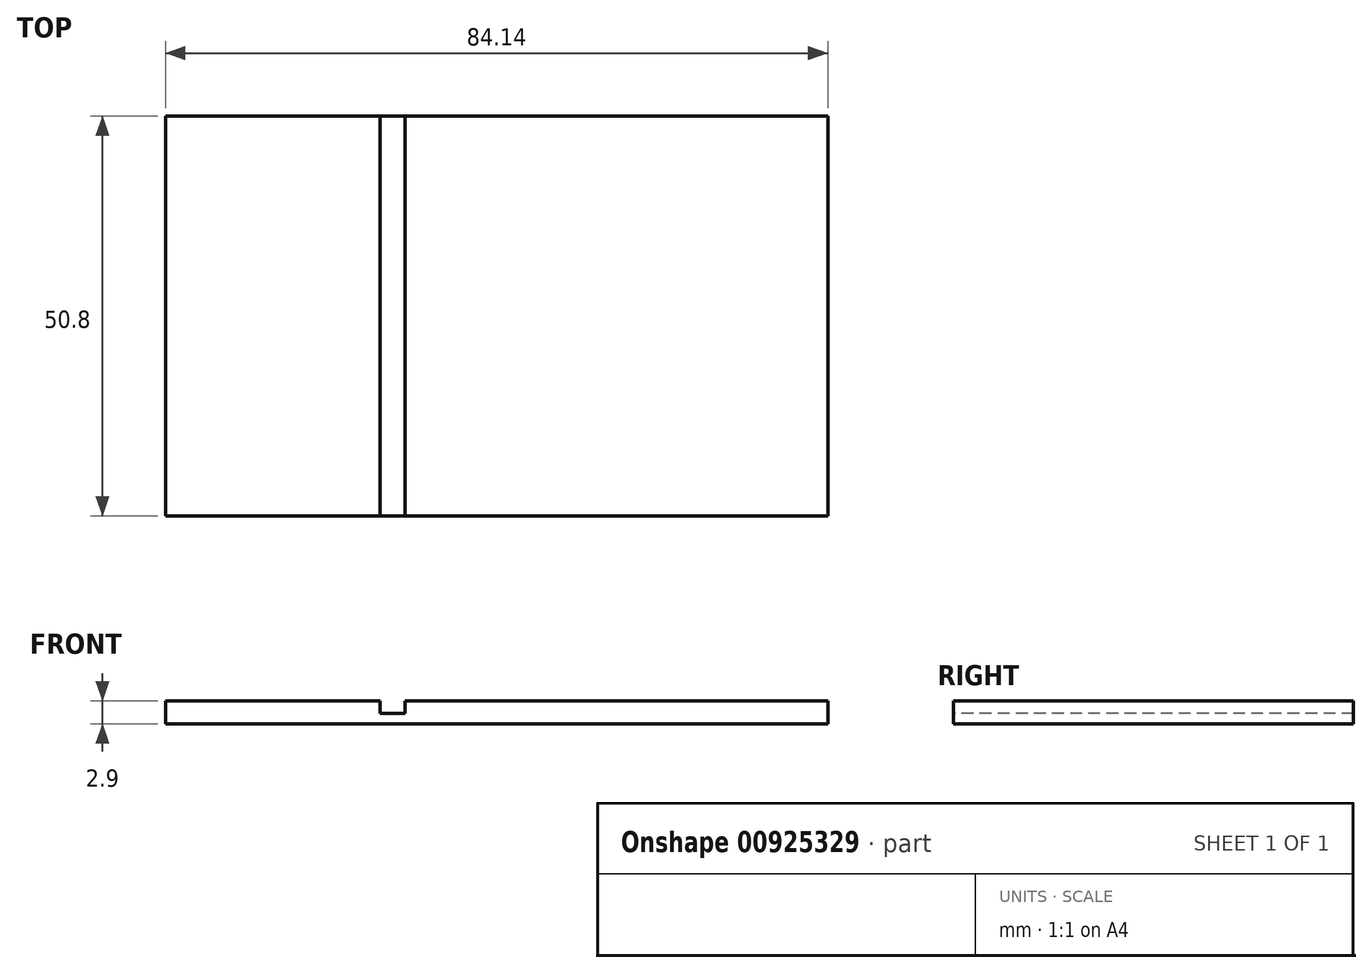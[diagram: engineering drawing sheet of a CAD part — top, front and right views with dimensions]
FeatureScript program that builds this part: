
annotation { "Feature Type Name" : "Feature", "Feature Type Description" : "" }
export const myFeature = defineFeature(function(context is Context, id is Id, definition is map)
    precondition{}
    {
        {
            var Q0;
            Q0=qCreatedBy(makeId("Top.planeOp"),FACE);
            var sketch = newSketch(context, id + "F0", { "sketchPlane" : qUnion([Q0])});
            skLineSegment(sketch, "E0.bottom", {"start": v(42.07, -25.4) * mm, "end": v(-42.07, -25.4) * mm});
            skLineSegment(sketch, "E0.top", {"start": v(42.07, 25.4) * mm, "end": v(-42.07, 25.4) * mm});
            skLineSegment(sketch, "E0.left", {"start": v(42.07, -25.4) * mm, "end": v(42.07, 25.4) * mm});
            skLineSegment(sketch, "E0.right", {"start": v(-42.07, -25.4) * mm, "end": v(-42.07, 25.4) * mm});
            skPoint(sketch, "E0.middle", {"position": v(0, 0) * mm});
            skSolve(sketch);
        }
        {
            var Q0;
            Q0=qSketchRegion(id+"F0",true);
            extrude(context, id + "F1", {"entities" : qUnion([Q0]), "depth" : 2.9 * mm, "offsetDistance" : 25.4 * mm});
        }
        {
            var Q0;
            Q0=makeQuery(id+"F1.opExtrude","CAP_FACE",FACE,{"disambiguationData":[OSD([sQuery(id+"F0.wireOp",EDGE,"E0.bottom"),sQuery(id+"F0.wireOp",EDGE,"E0.top"),sQuery(id+"F0.wireOp",EDGE,"E0.left"),sQuery(id+"F0.wireOp",EDGE,"E0.right")])],"isStart":false});
            var sketch = newSketch(context, id + "F2", { "sketchPlane" : qUnion([Q0])});
            skLineSegment(sketch, "E1.bottom", {"start": v(-14.83, 25.4) * mm, "end": v(-11.65, 25.4) * mm});
            skLineSegment(sketch, "E1.top", {"start": v(-14.83, -25.4) * mm, "end": v(-11.65, -25.4) * mm});
            skLineSegment(sketch, "E1.left", {"start": v(-14.83, 25.4) * mm, "end": v(-14.83, -25.4) * mm});
            skLineSegment(sketch, "E1.right", {"start": v(-11.65, 25.4) * mm, "end": v(-11.65, -25.4) * mm});
            skSolve(sketch);
        }
        {
            var Q0;
            Q0=qSketchRegion(id+"F2",true);
            extrude(context, id + "F3", {"entities" : qUnion([Q0]), "operationType" : NewBodyOperationType.REMOVE, "oppositeDirection" : true, "depth" : 1.59 * mm, "offsetDistance" : 25.4 * mm});
        }
    });
